# Revit family: Door-StormDefender-FaceOfWallMount_Cookson
name_source: partatom
category: Doors
revit_build: Autodesk Revit 2018 (Build: 20170223_1515(x64)
units: mm (PartAtom-declared; Revit-internal decimal feet)

## family parameters
Always vertical = Yes
Cut with Voids When Loaded = No
Host = Wall
OmniClass Number = 23.30.10.17.27.11
OmniClass Title = Overhead Coiling
Room Calculation Point = No
Shared = No

## types (1)
- Door-StormDefender-FaceOfWallMount_Cookson
    # Of Slats = 50
    04 CSI = 08 33 00
    95 CSI = 08330
    A Coil Hood Height = 2' - 5"
    Analytic Construction = <None>
    Assembly Code = B2030410
    B Coil Hood Depth = 2' - 5"
    C = 5 1/2"
    CAD Resources = https://www.cooksondoor.com
    Clearances on Adjuster side Note = 6In - 8In wide. Consult Cookson when dimensions are critical.
    Clearances on Operator side Note = 9In-11In wide. Consult Cookson when dimensions are critical.
    Coil Dimension Note = Consult Cornell when dimensions are critical.
    Cookson Products = https://www.cooksondoor.com
    Cookson Projects = https://www.cooksondoor.com
    Cost = 0 $
    Cost Note = Based on size, materials selected. Consult Cookson.
    D = 3 1/2"
    Description = StormDefender is designed specifically to protect life in safe rooms for hurricanes and tornados. It is certified to stringent ICC500-2014 and FEMA P-361, Third Edition code standards, and connects directly to the building's alarm ssytem, ensuring the door deploys on alarm. The door is completely recessed in the ceiling, allowing complete design freedom for Safe Rooms in public institutions. A listed fire rated version is also available.
    Distributor Locator = https://www.cooksondoor.com
    E = 7 3/8"
    Function = Interior
    Guard Width = 14' - 3 1/4"
    Guide Height = 16' - 9"
    Height = 19' - 2"
    Jamb Dimension Note = 4 - 8In wide and 5-6In deep. Consult Cookson when dimensions are critical.
    LEED Information = https://www.cooksondoor.com
    Listings = ICC 500 - 2014, FEMA P-361, [UL10B, UL1784 (fire rated model only)]
    Manufacturer = Cookson:  1901 Litchfield Road, Goodyear, AZ 85338.  Telephone: (800) 294-4358
    Model = PRSD361
    Mounting = Face of Wall
    Non-Fire-Rated (PSD361) = No
    Opening Height = 16' - 0"
    Opening Width = 14' - 0"
    Operation = Motor Operator
    Operator Height = 5' - 4"
    Operator Left Side Horizontal OR = No
    Operator Left Side Top OR = No
    Operator Right Side Horizontal OR = No
    Operator Right Side Top OR = Yes
    Operator Width = 14' - 9"
    Operator on Left = No
    Operator on Right = Yes
    Product Options = Seismic Performance Validation. Standard Emergency Annuciator: [ADA Compliant horn/strobe.  Voice Warning Module                                 
Standard : Emergency Annunciator: [ADA compliant horn/strobe] [Voice Warning Module] emergency annunciator to give advanced warning that door is about to close, activating warning signal upon alarm or activation. 
Standard : Battery Back-Up: Model R-BBU Battery Back-Up System for AlarmGard Motor Operator: Prevent gravity closure for a minimum of four hours due to power failure.
Operator and Full Bracket Mechanism Cover: Provide minimum 24 gauge [galvanized steel] [stainless steel] sheet metal cover [to provide weather resistance] [to enclose exposed moving operating components] at coil area of unit. Finish to match door hood.
    Product Page = https://www.cooksondoor.com
    Rating Offset = 5"
    Representative Disclaimer = Cookson products are sold and installed through a nationwide network of independent distributors.
    Rough Height = 7' - 10 1/2"
    Sizing for Opening Size = Minimum 3ft x 3ft and Max Openings up to 14ft wide x 16ft high
    Specifications = https://www.cooksondoor.com
    Subcategory = Roll Up
    URL = https://www.cooksondoor.com
    Wall Closure = By host
    Wall Construction = Steel or Masonry
    Width = 14' - 0"

## geometry (parser evidence)
native form markers: Blend x8, Sweep x17
no freeform markers — native parametric forms only
